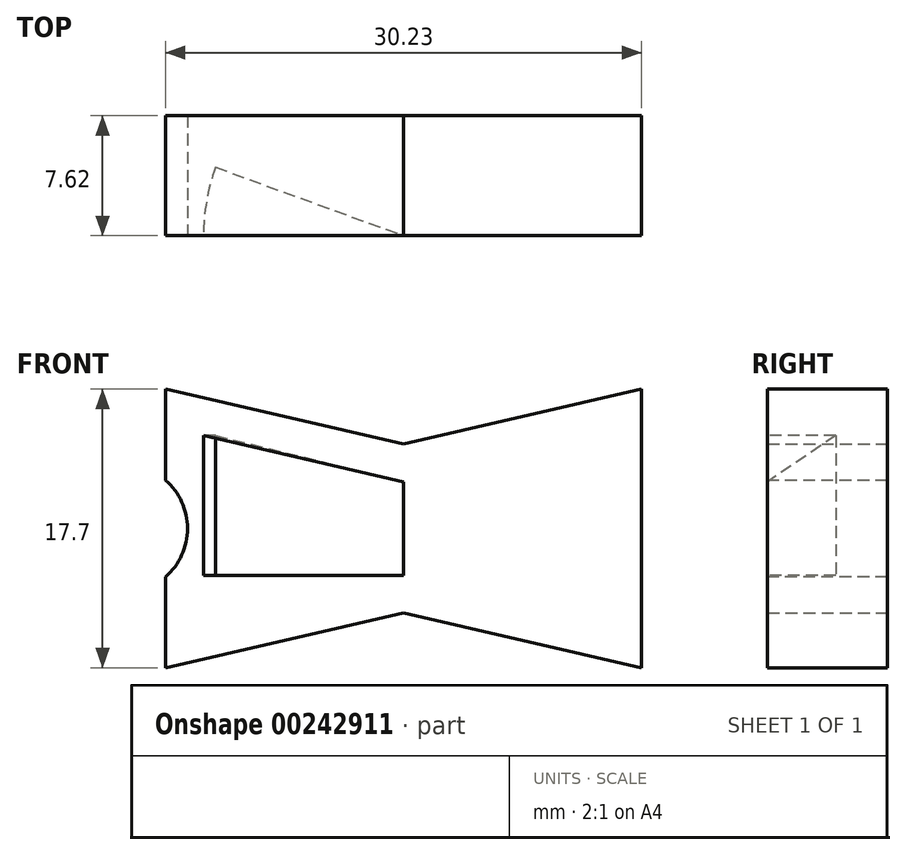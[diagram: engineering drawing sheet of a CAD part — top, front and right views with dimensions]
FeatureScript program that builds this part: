
annotation { "Feature Type Name" : "Feature", "Feature Type Description" : "" }
export const myFeature = defineFeature(function(context is Context, id is Id, definition is map)
    precondition{}
    {
        {
            var Q0;
            Q0=qCreatedBy(makeId("Front.planeOp"),FACE);
            var sketch = newSketch(context, id + "F0", { "sketchPlane" : qUnion([Q0])});
            skLineSegment(sketch, "E0.bottom", {"start": v(0, 0) * mm, "end": v(31.75, 0) * mm});
            skLineSegment(sketch, "E0.top", {"start": v(0, -19.62) * mm, "end": v(31.75, -19.62) * mm});
            skLineSegment(sketch, "E0.left", {"start": v(0, 0) * mm, "end": v(0, -19.62) * mm});
            skLineSegment(sketch, "E0.right", {"start": v(31.75, 0) * mm, "end": v(31.75, -19.62) * mm});
            skLineSegment(sketch, "E1", {"start": v(15.88, 0) * mm, "end": v(15.88, -19.62) * mm});
            skLineSegment(sketch, "E2", {"start": v(0, -19.62) * mm, "end": v(15.88, -15.96) * mm});
            skLineSegment(sketch, "E3", {"start": v(15.88, -15.96) * mm, "end": v(31.75, -19.62) * mm});
            skLineSegment(sketch, "E4", {"start": v(31.75, 0) * mm, "end": v(15.88, -3.67) * mm});
            skLineSegment(sketch, "E5", {"start": v(15.88, -3.67) * mm, "end": v(0, 0) * mm});
            skSolve(sketch);
        }
        {
            var Q0;
            Q0=makeQuery(id+"F0.imprint","IMPRINT",FACE,{"disambiguationData":[TD([[makeQuery(id+"F0.imprint","IMPRINT",EDGE,{"derivedFrom":sQuery(id+"F0.wireOp",EDGE,"E0.left")}),1.0]])]});
            var Q1;
            Q1=makeQuery(id+"F0.imprint","IMPRINT",FACE,{"disambiguationData":[TD([[makeQuery(id+"F0.imprint","IMPRINT",EDGE,{"derivedFrom":sQuery(id+"F0.wireOp",EDGE,"E0.right")}),-1.0]])]});
            extrude(context, id + "F1", {"entities" : qUnion([Q0, Q1]), "depth" : 7.62 * mm});
        }
        {
            var Q0;
            Q0=makeQuery(id+"F1.opExtrude","CAP_FACE",FACE,{"disambiguationData":[OSD([sQuery(id+"F0.wireOp",EDGE,"E0.left"),sQuery(id+"F0.wireOp",EDGE,"E0.right"),sQuery(id+"F0.wireOp",EDGE,"E2"),sQuery(id+"F0.wireOp",EDGE,"E3"),sQuery(id+"F0.wireOp",EDGE,"E4"),sQuery(id+"F0.wireOp",EDGE,"E5")])],"isStart":false});
            var sketch = newSketch(context, id + "F2", { "sketchPlane" : qUnion([Q0])});
            skLineSegment(sketch, "E6.bottom", {"start": v(3.17, -6.84) * mm, "end": v(15.87, -6.84) * mm});
            skLineSegment(sketch, "E6.top", {"start": v(3.17, -12.78) * mm, "end": v(15.88, -12.78) * mm});
            skLineSegment(sketch, "E6.left", {"start": v(3.17, -6.84) * mm, "end": v(3.17, -12.78) * mm});
            skLineSegment(sketch, "E6.right", {"start": v(15.88, -6.84) * mm, "end": v(15.88, -12.78) * mm});
            skLineSegment(sketch, "E7", {"start": v(15.88, -12.78) * mm, "end": v(3.17, -12.78) * mm});
            skLineSegment(sketch, "E8", {"start": v(3.17, -12.78) * mm, "end": v(3.17, -15.71) * mm});
            skLineSegment(sketch, "E9", {"start": v(3.17, -15.71) * mm, "end": v(15.88, -12.78) * mm});
            skLineSegment(sketch, "E10", {"start": v(3.17, -6.84) * mm, "end": v(3.17, -3.9) * mm});
            skLineSegment(sketch, "E11", {"start": v(3.17, -3.9) * mm, "end": v(15.87, -6.84) * mm});
            skLineSegment(sketch, "E12", {"start": v(15.88, -3.67) * mm, "end": v(15.88, -15.96) * mm});
            skSolve(sketch);
        }
        {
            var Q0;
            {var subQ0=sQuery(id+"F2.wireOp",EDGE,"E6.bottom");Q0=makeQuery(id+"F2.imprint","IMPRINT",FACE,{"disambiguationData":[TD([[makeQuery(id+"F2.imprint","IMPRINT",EDGE,{"derivedFrom":subQ0}),-1.0]])]});}
            var Q1;
            Q1=makeQuery(id+"F2.imprint","IMPRINT",FACE,{"disambiguationData":[TD([[makeQuery(id+"F2.imprint","IMPRINT",EDGE,{"derivedFrom":sQuery(id+"F2.wireOp",EDGE,"E7")}),1.0]])]});
            var Q2;
            Q2=makeQuery(id+"F2.imprint","IMPRINT",FACE,{"disambiguationData":[TD([[makeQuery(id+"F2.imprint","IMPRINT",EDGE,{"derivedFrom":sQuery(id+"F2.wireOp",EDGE,"E6.bottom")}),1.0]])]});
            var Q3;
            Q3=sQuery(id+"F2.wireOp",EDGE,"E12");
            revolve(context, id + "F3", {"operationType" : NewBodyOperationType.REMOVE, "entities" : qUnion([Q0, Q1, Q2]), "axis" : qUnion([Q3]), "revolveType" : RevolveType.ONE_DIRECTION, "angle" : 20 * degree});
        }
        {
            var Q0;
            Q0=makeQuery(id+"F1.opExtrude","CAP_FACE",FACE,{"disambiguationData":[OSD([sQuery(id+"F0.wireOp",EDGE,"E0.left"),sQuery(id+"F0.wireOp",EDGE,"E0.right"),sQuery(id+"F0.wireOp",EDGE,"E2"),sQuery(id+"F0.wireOp",EDGE,"E3"),sQuery(id+"F0.wireOp",EDGE,"E4"),sQuery(id+"F0.wireOp",EDGE,"E5")])],"isStart":true});
            var sketch = newSketch(context, id + "F4", { "sketchPlane" : qUnion([Q0])});
            skLineSegment(sketch, "E13", {"start": v(-30.99, -18.66) * mm, "end": v(-30.99, -0.96) * mm});
            skLineSegment(sketch, "E14", {"start": v(-30.99, -0.96) * mm, "end": v(-15.88, -4.45) * mm});
            skLineSegment(sketch, "E15", {"start": v(-15.88, -4.45) * mm, "end": v(-0.76, -0.96) * mm});
            skLineSegment(sketch, "E16", {"start": v(-0.76, -0.96) * mm, "end": v(-0.76, -18.66) * mm});
            skLineSegment(sketch, "E17", {"start": v(-0.76, -18.66) * mm, "end": v(-15.88, -15.18) * mm});
            skLineSegment(sketch, "E18", {"start": v(-15.88, -15.18) * mm, "end": v(-30.99, -18.66) * mm});
            skSolve(sketch);
        }
        {
            var Q0;
            Q0=makeQuery(id+"F4.imprint","IMPRINT",FACE,{"disambiguationData":[TD([[makeQuery(id+"F4.imprint","IMPRINT",EDGE,{"derivedFrom":sQuery(id+"F4.wireOp",EDGE,"E13")}),1.0]])]});
            extrude(context, id + "F5", {"entities" : qUnion([Q0]), "operationType" : NewBodyOperationType.REMOVE, "oppositeDirection" : true, "depth" : 25.4 * mm});
        }
        {
            var Q0;
            Q0=makeQuery(id+"F1.opExtrude","CAP_FACE",FACE,{"disambiguationData":[OSD([sQuery(id+"F0.wireOp",EDGE,"E0.left"),sQuery(id+"F0.wireOp",EDGE,"E0.right"),sQuery(id+"F0.wireOp",EDGE,"E2"),sQuery(id+"F0.wireOp",EDGE,"E3"),sQuery(id+"F0.wireOp",EDGE,"E4"),sQuery(id+"F0.wireOp",EDGE,"E5")])],"isStart":false});
            var sketch = newSketch(context, id + "F6", { "sketchPlane" : qUnion([Q0])});
            skLineSegment(sketch, "E19", {"start": v(0.76, -18.66) * mm, "end": v(0.76, -0.96) * mm});
            skLineSegment(sketch, "E20", {"start": v(0.76, -0.96) * mm, "end": v(0.76, -9.81) * mm});
            skLineSegment(sketch, "E21", {"start": v(0.76, -9.81) * mm, "end": v(3.17, -9.81) * mm});
            skCircle(sketch, "E22", {"center": v(-1.9, -9.81) * mm, "radius": 4.06 * mm});
            skSolve(sketch);
        }
        {
            var Q0;
            {var subQ1=sQuery(id+"F6.wireOp",EDGE,"E19");var subQ3=sQuery(id+"F6.wireOp",EDGE,"E22");var subQ4=makeQuery(id+"F6.imprint","INTERSECT",VERTEX,{"derivedFrom":[subQ1,subQ3]});Q0=makeQuery(id+"F6.imprint","IMPRINT",FACE,{"disambiguationData":[TD([[makeQuery(id+"F6.imprint","IMPRINT",EDGE,{"disambiguationData":[TD([[subQ4,-1.0]])],"derivedFrom":subQ3}),1.0]])]});}
            var Q1;
            {var subQ1=sQuery(id+"F6.wireOp",EDGE,"E20");var subQ3=sQuery(id+"F6.wireOp",EDGE,"E22");var subQ4=makeQuery(id+"F6.imprint","INTERSECT",VERTEX,{"derivedFrom":[subQ1,subQ3]});Q1=makeQuery(id+"F6.imprint","IMPRINT",FACE,{"disambiguationData":[TD([[makeQuery(id+"F6.imprint","IMPRINT",EDGE,{"disambiguationData":[TD([[subQ4,1.0]])],"derivedFrom":subQ3}),1.0]])]});}
            extrude(context, id + "F7", {"entities" : qUnion([Q0, Q1]), "operationType" : NewBodyOperationType.REMOVE, "oppositeDirection" : true, "depth" : 25.4 * mm});
        }
    });
